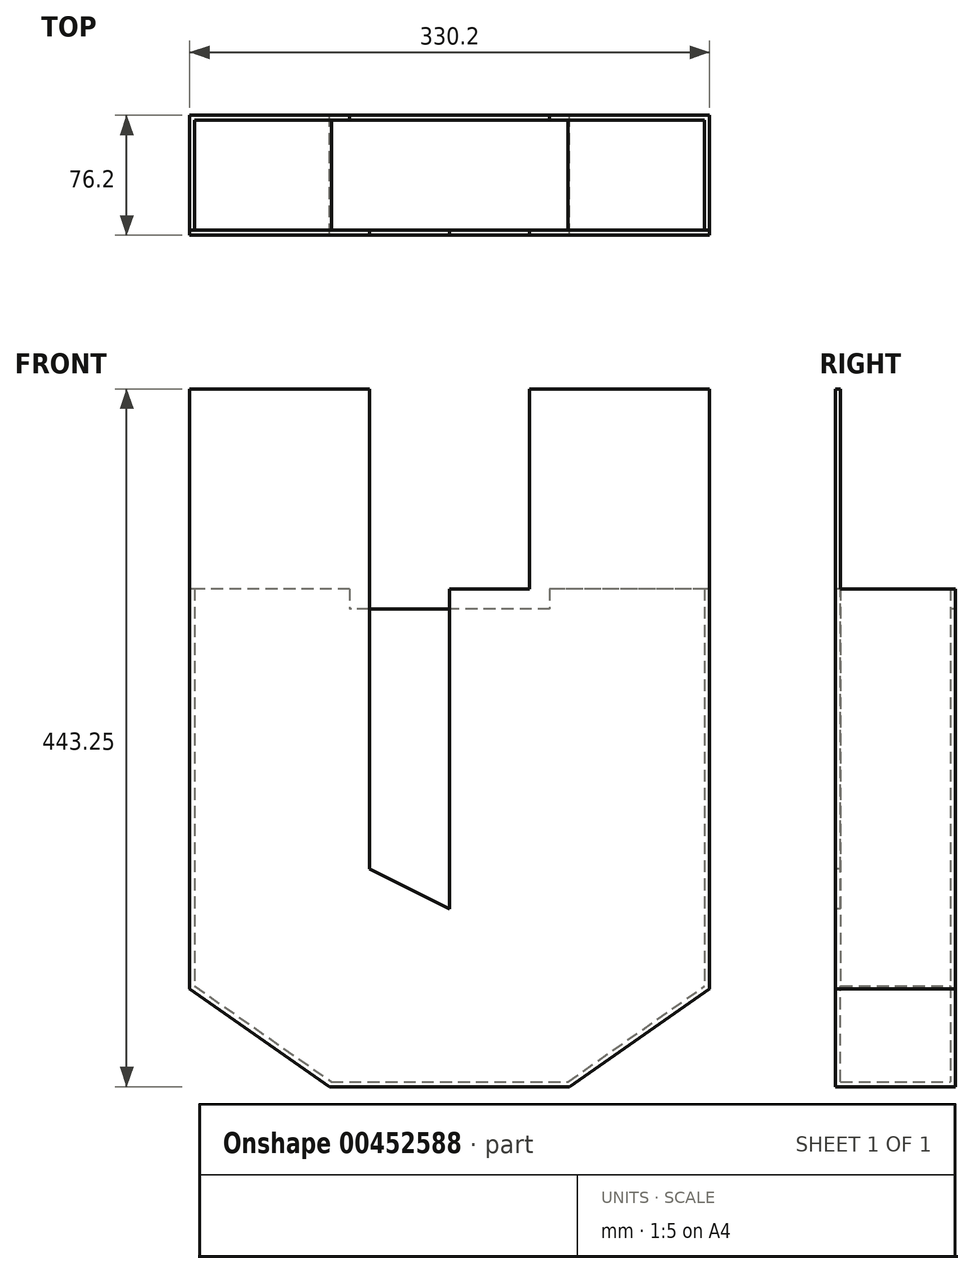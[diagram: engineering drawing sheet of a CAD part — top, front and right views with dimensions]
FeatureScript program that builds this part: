
annotation { "Feature Type Name" : "Feature", "Feature Type Description" : "" }
export const myFeature = defineFeature(function(context is Context, id is Id, definition is map)
    precondition{}
    {
        {
            var Q0;
            Q0=qCreatedBy(makeId("Front.planeOp"),FACE);
            var sketch = newSketch(context, id + "F0", { "sketchPlane" : qUnion([Q0])});
            skCircle(sketch, "E0", {"center": v(0, 0) * mm, "radius": 127 * mm});
            skLineSegment(sketch, "E1.bottom", {"start": v(165.1, 127) * mm, "end": v(-165.1, 127) * mm});
            skLineSegment(sketch, "E1.top", {"start": v(165.1, -127) * mm, "end": v(-165.1, -127) * mm});
            skLineSegment(sketch, "E1.left", {"start": v(165.1, 127) * mm, "end": v(165.1, -127) * mm});
            skLineSegment(sketch, "E1.right", {"start": v(-165.1, 127) * mm, "end": v(-165.1, -127) * mm});
            skLineSegment(sketch, "E2", {"start": v(-165.1, -127) * mm, "end": v(-76.2, -189.25) * mm});
            skLineSegment(sketch, "E3", {"start": v(-76.2, -189.25) * mm, "end": v(76.2, -189.25) * mm});
            skLineSegment(sketch, "E4", {"start": v(76.2, -189.25) * mm, "end": v(165.1, -127) * mm});
            skSolve(sketch);
        }
        {
            var Q0;
            Q0=qSketchRegion(id+"F0",true);
            var Q1;
            Q1=makeQuery(id+"F0.imprint","IMPRINT",FACE,{"disambiguationData":[TD([[makeQuery(id+"F0.imprint","IMPRINT",EDGE,{"derivedFrom":sQuery(id+"F0.wireOp",EDGE,"E0")}),1.0]])]});
            extrude(context, id + "F1", {"entities" : qUnion([Q0, Q1]), "depth" : 76.2 * mm});
        }
        {
            var Q0;
            Q0=makeQuery(id+"F1.opExtrude","SWEPT_FACE",FACE,{"disambiguationData":[OSD([sQuery(id+"F0.wireOp",EDGE,"E1.bottom")])]});
            shell(context, id + "F2", {"entities" : qUnion([Q0]), "thickness" : 3.17 * mm});
        }
        {
            var Q0;
            Q0=makeQuery(id+"F1.opExtrude","CAP_FACE",FACE,{"disambiguationData":[OSD([sQuery(id+"F0.wireOp",EDGE,"E1.bottom"),sQuery(id+"F0.wireOp",EDGE,"E1.top"),sQuery(id+"F0.wireOp",EDGE,"E1.left"),sQuery(id+"F0.wireOp",EDGE,"E1.right")])],"isStart":false});
            var sketch = newSketch(context, id + "F3", { "sketchPlane" : qUnion([Q0])});
            skLineSegment(sketch, "E5", {"start": v(0, 127) * mm, "end": v(0, -76.2) * mm});
            skPoint(sketch, "E5.endSnap0", {"position": v(0, 127) * mm});
            skLineSegment(sketch, "E6", {"start": v(0, -76.2) * mm, "end": v(-50.8, -50.8) * mm});
            skLineSegment(sketch, "E7", {"start": v(-50.8, -50.8) * mm, "end": v(-50.8, 127) * mm});
            skSolve(sketch);
        }
        {
            var Q0;
            {var subQ0=sQuery(id+"F3.wireOp",EDGE,"E5");Q0=makeQuery(id+"F3.imprint","IMPRINT",FACE,{"disambiguationData":[TD([[makeQuery(id+"F3.imprint","IMPRINT",EDGE,{"derivedFrom":subQ0}),-1.0]])]});}
            extrude(context, id + "F4", {"entities" : qUnion([Q0]), "operationType" : NewBodyOperationType.REMOVE, "oppositeDirection" : true, "depth" : 25.4 * mm});
        }
        {
            var Q0;
            {var subQ0=sQuery(id+"F0.wireOp",EDGE,"E4");var subQ1=sQuery(id+"F0.wireOp",EDGE,"E3");var subQ2=sQuery(id+"F0.wireOp",EDGE,"E2");var subQ3=sQuery(id+"F0.wireOp",EDGE,"E1.right");var subQ4=sQuery(id+"F0.wireOp",EDGE,"E1.left");var subQ5=sQuery(id+"F0.wireOp",EDGE,"E1.bottom");Q0=makeQuery(id+"F2.opShell","OFFSET_FACE",FACE,{"disambiguationData":[OSD([subQ5,subQ4,subQ3,subQ2,subQ1,subQ0]),TDD([makeQuery(id+"F1.opExtrude","CAP_FACE",FACE,{"disambiguationData":[OSD([subQ5,subQ4,subQ3,subQ2,subQ1,subQ0])],"isStart":true})])]});}
            var sketch = newSketch(context, id + "F5", { "sketchPlane" : qUnion([Q0])});
            skLineSegment(sketch, "E8.bottom", {"start": v(63.5, 139.7) * mm, "end": v(-63.5, 139.7) * mm});
            skLineSegment(sketch, "E8.top", {"start": v(63.5, 114.3) * mm, "end": v(-63.5, 114.3) * mm});
            skLineSegment(sketch, "E8.left", {"start": v(63.5, 139.7) * mm, "end": v(63.5, 114.3) * mm});
            skLineSegment(sketch, "E8.right", {"start": v(-63.5, 139.7) * mm, "end": v(-63.5, 114.3) * mm});
            skPoint(sketch, "E8.middle", {"position": v(0, 127) * mm});
            skSolve(sketch);
        }
        {
            var Q0;
            Q0=qSketchRegion(id+"F5",true);
            extrude(context, id + "F6", {"entities" : qUnion([Q0]), "operationType" : NewBodyOperationType.REMOVE, "oppositeDirection" : true, "depth" : 25.4 * mm});
        }
        {
            var Q0;
            Q0=makeQuery(id+"F1.opExtrude","CAP_FACE",FACE,{"disambiguationData":[OSD([sQuery(id+"F0.wireOp",EDGE,"E1.bottom"),sQuery(id+"F0.wireOp",EDGE,"E1.left"),sQuery(id+"F0.wireOp",EDGE,"E1.right"),sQuery(id+"F0.wireOp",EDGE,"E2"),sQuery(id+"F0.wireOp",EDGE,"E3"),sQuery(id+"F0.wireOp",EDGE,"E4")])],"isStart":false});
            var sketch = newSketch(context, id + "F7", { "sketchPlane" : qUnion([Q0])});
            skLineSegment(sketch, "E9.bottom", {"start": v(-165.1, 127) * mm, "end": v(165.1, 127) * mm});
            skLineSegment(sketch, "E9.top", {"start": v(-165.1, 254) * mm, "end": v(165.1, 254) * mm});
            skLineSegment(sketch, "E9.left", {"start": v(-165.1, 127) * mm, "end": v(-165.1, 254) * mm});
            skLineSegment(sketch, "E9.right", {"start": v(165.1, 127) * mm, "end": v(165.1, 254) * mm});
            skSolve(sketch);
        }
        {
            var Q0;
            Q0=qSketchRegion(id+"F7",true);
            extrude(context, id + "F8", {"entities" : qUnion([Q0]), "operationType" : NewBodyOperationType.ADD, "oppositeDirection" : true, "depth" : 3.17 * mm});
        }
        {
            var Q0;
            Q0=makeQuery(id+"F8.boolean.opBoolean","MERGE",FACE,{"derivedFrom":[makeQuery(id+"F1.opExtrude","CAP_FACE",FACE,{"disambiguationData":[OSD([sQuery(id+"F0.wireOp",EDGE,"E1.bottom"),sQuery(id+"F0.wireOp",EDGE,"E1.left"),sQuery(id+"F0.wireOp",EDGE,"E1.right"),sQuery(id+"F0.wireOp",EDGE,"E2"),sQuery(id+"F0.wireOp",EDGE,"E3"),sQuery(id+"F0.wireOp",EDGE,"E4")])],"isStart":false}),makeQuery(id+"F8.opExtrude","CAP_FACE",FACE,{"disambiguationData":[OSD([sQuery(id+"F7.wireOp",EDGE,"E9.bottom"),sQuery(id+"F7.wireOp",EDGE,"E9.top"),sQuery(id+"F7.wireOp",EDGE,"E9.left"),sQuery(id+"F7.wireOp",EDGE,"E9.right")])],"isStart":true})]});
            var sketch = newSketch(context, id + "F9", { "sketchPlane" : qUnion([Q0])});
            skLineSegment(sketch, "E10.bottom", {"start": v(-50.8, 127) * mm, "end": v(50.8, 127) * mm});
            skLineSegment(sketch, "E10.top", {"start": v(-50.8, 254) * mm, "end": v(50.8, 254) * mm});
            skLineSegment(sketch, "E10.left", {"start": v(-50.8, 127) * mm, "end": v(-50.8, 254) * mm});
            skLineSegment(sketch, "E10.right", {"start": v(50.8, 127) * mm, "end": v(50.8, 254) * mm});
            skSolve(sketch);
        }
        {
            var Q0;
            Q0=qSketchRegion(id+"F9",true);
            extrude(context, id + "F10", {"entities" : qUnion([Q0]), "operationType" : NewBodyOperationType.REMOVE, "oppositeDirection" : true, "depth" : 25.4 * mm});
        }
    });
